# Revit family: 3503A_NX_In_Fixture_Module_Offset
name_source: partatom
category: Communication Devices
revit_build: Autodesk Revit 2014 (Build: 20130308_1515(x64)
units: mm (PartAtom-declared; Revit-internal decimal feet)

## types (1)
- 3503A_NX_In_Fixture_Module_Offset
    Apparent Load = 0 VA
    Assembly Code = D5090
    Black Element = Paint - Hubbell - Carbon Black
    Certifications = Conforms with UL916 and Certified to CAN/CSA C22.2 No. 205-M1983
IC Approved
    Default Elevation = 48 "
    Description = It enables a complete control solution for a single luminaire
    Electrical Ratings = Input: 120-347VAC, 10A Max, 50-60Hz
Output: 10A, 120VAC only, Incandescent
 10A, 120-347VAC, Magnetic Ballast
 5A, 120-277VAC, Electronic Ballast
 3A, 347VAC, Electronic Ballast
Surge Withstand: 2000V
Peak Inrush: 160A for 2ms Max
    Features = • Designed for installation within luminaire housing
• Universal Voltage, 120-347V
• Mounting tray with snap in/snap out feature
• Space saving offset flying leads
• Integral relay for On/Off control
• Continuous dimming 0-10 volt control
• Second dimming channel for variable color temperature
• Compatible with SpectraSync™ enabled luminaires
• Wireless programming via free Smart Device App*
• SmartPORT™ technology for plug-in control and radio options
• Suitable for indoor and outdoor applications
    Housing Material = Metal-Hubbell-Aluminum Anodized Blue
    Manufacturer = Hubbell Control Solutions
    Model = NXFM series in-fixture module
    Product Documentation Link = https://hubbellcdn.com
    Product Page URL = https://www.hubbell.com
    Type Comments = In-Fixture Module -Low Voltage
    URL = https://www.hubbell.com
    Voltage = 10 V
    Warranty = 5-Years Warranty

## geometry (parser evidence)
native form markers: Sweep x1
no freeform markers — native parametric forms only
